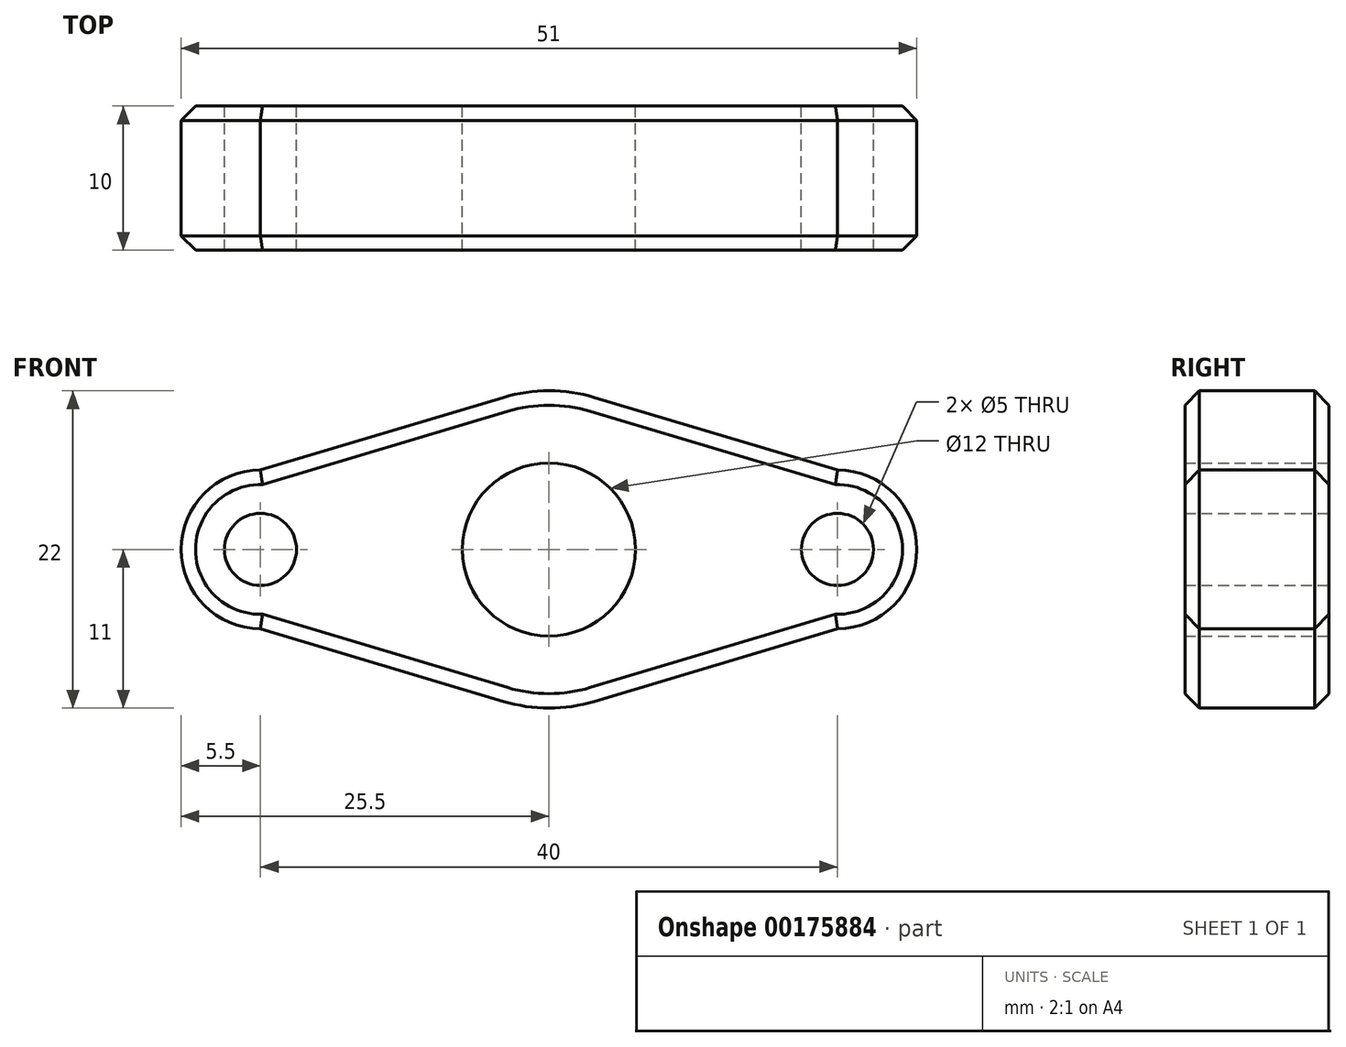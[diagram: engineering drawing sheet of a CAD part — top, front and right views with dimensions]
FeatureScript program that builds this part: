
annotation { "Feature Type Name" : "Feature", "Feature Type Description" : "" }
export const myFeature = defineFeature(function(context is Context, id is Id, definition is map)
    precondition{}
    {
        {
            var Q0;
            Q0=qCreatedBy(makeId("Front.planeOp"),FACE);
            var sketch = newSketch(context, id + "F0", { "sketchPlane" : qUnion([Q0])});
            skCircle(sketch, "E0", {"center": v(0, 0) * mm, "radius": 6 * mm});
            skCircle(sketch, "E1", {"center": v(20, 0) * mm, "radius": 2.5 * mm});
            skArc(sketch, "E2", {"start": v(20, 5.5) * mm, "mid": v(25.5, 0) * mm, "end": v(20, -5.5) * mm});
            skArc(sketch, "E3", {"start": v(0, 11) * mm, "mid": v(1.6, 10.88) * mm, "end": v(3.15, 10.54) * mm});
            skArc(sketch, "E4", {"start": v(0, -11) * mm, "mid": v(1.6, -10.88) * mm, "end": v(3.15, -10.54) * mm});
            skLineSegment(sketch, "E5", {"start": v(3.15, 10.54) * mm, "end": v(20, 5.5) * mm});
            skLineSegment(sketch, "E6", {"start": v(20, -5.5) * mm, "end": v(3.15, -10.54) * mm});
            skArc(sketch, "E7.MirrorCS", {"start": v(0, 11) * mm, "mid": v(-1.6, 10.88) * mm, "end": v(-3.15, 10.54) * mm});
            skArc(sketch, "E8.MirrorCS", {"start": v(0, -11) * mm, "mid": v(-1.6, -10.88) * mm, "end": v(-3.15, -10.54) * mm});
            skLineSegment(sketch, "E9.MirrorCS", {"start": v(-3.15, 10.54) * mm, "end": v(-20, 5.5) * mm});
            skCircle(sketch, "E10.MirrorC", {"center": v(-20, 0) * mm, "radius": 2.5 * mm});
            skArc(sketch, "E11.MirrorCS", {"start": v(-20, 5.5) * mm, "mid": v(-25.5, 0) * mm, "end": v(-20, -5.5) * mm});
            skLineSegment(sketch, "E12.MirrorCS", {"start": v(-20, -5.5) * mm, "end": v(-3.15, -10.54) * mm});
            skSolve(sketch);
        }
        {
            var Q0;
            Q0 = qSketchRegion(id + "F0", true);
            extrude(context, id + "F1", {"entities" : qUnion([Q0]), "endBound" : BoundingType.SYMMETRIC, "depth" : 10 * mm});
        }
        {
            var Q0;
            Q0=makeQuery(id+"F1.opExtrude","CAP_EDGE",EDGE,{"disambiguationData":[OSD([sQuery(id+"F0.wireOp",EDGE,"E9.MirrorCS")])],"isStart":false});
            var Q1;
            Q1=makeQuery(id+"F1.opExtrude","CAP_EDGE",EDGE,{"disambiguationData":[OSD([sQuery(id+"F0.wireOp",EDGE,"E2")])],"isStart":false});
            var Q2;
            Q2=makeQuery(id+"F1.opExtrude","CAP_EDGE",EDGE,{"disambiguationData":[OSD([sQuery(id+"F0.wireOp",EDGE,"E5")])],"isStart":false});
            var Q3;
            Q3=makeQuery(id+"F1.opExtrude","CAP_EDGE",EDGE,{"disambiguationData":[OSD([sQuery(id+"F0.wireOp",EDGE,"E3"),sQuery(id+"F0.wireOp",EDGE,"E7.MirrorCS")])],"isStart":false});
            var Q4;
            Q4=makeQuery(id+"F1.opExtrude","CAP_EDGE",EDGE,{"disambiguationData":[OSD([sQuery(id+"F0.wireOp",EDGE,"E6")])],"isStart":false});
            var Q5;
            Q5=makeQuery(id+"F1.opExtrude","CAP_EDGE",EDGE,{"disambiguationData":[OSD([sQuery(id+"F0.wireOp",EDGE,"E11.MirrorCS")])],"isStart":false});
            var Q6;
            Q6=makeQuery(id+"F1.opExtrude","CAP_EDGE",EDGE,{"disambiguationData":[OSD([sQuery(id+"F0.wireOp",EDGE,"E11.MirrorCS")])],"isStart":true});
            var Q7;
            Q7=makeQuery(id+"F1.opExtrude","CAP_EDGE",EDGE,{"disambiguationData":[OSD([sQuery(id+"F0.wireOp",EDGE,"E2")])],"isStart":true});
            var Q8;
            Q8=makeQuery(id+"F1.opExtrude","CAP_EDGE",EDGE,{"disambiguationData":[OSD([sQuery(id+"F0.wireOp",EDGE,"E5")])],"isStart":true});
            var Q9;
            Q9=makeQuery(id+"F1.opExtrude","CAP_EDGE",EDGE,{"disambiguationData":[OSD([sQuery(id+"F0.wireOp",EDGE,"E9.MirrorCS")])],"isStart":true});
            var Q10;
            Q10=makeQuery(id+"F1.opExtrude","CAP_EDGE",EDGE,{"disambiguationData":[OSD([sQuery(id+"F0.wireOp",EDGE,"E12.MirrorCS")])],"isStart":true});
            var Q11;
            Q11=makeQuery(id+"F1.opExtrude","CAP_EDGE",EDGE,{"disambiguationData":[OSD([sQuery(id+"F0.wireOp",EDGE,"E6")])],"isStart":true});
            chamfer(context, id + "F2", {"entities" : qUnion([Q0, Q1, Q2, Q3, Q4, Q5, Q6, Q7, Q8, Q9, Q10, Q11]), "width" : 1 * mm, "tangentPropagation" : true});
        }
    });
